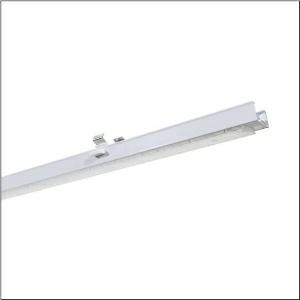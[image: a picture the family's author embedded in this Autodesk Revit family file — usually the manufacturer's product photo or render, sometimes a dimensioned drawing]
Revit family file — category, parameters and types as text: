
# Revit family: trunking_flex_31_51re11db49b
name_source: partatom
category: Lighting Fixtures
units: mm (PartAtom-declared; Revit-internal decimal feet)

## family parameters
Cut with Voids When Loaded = No
Host = Face
Light Source = No
Part Type = Normal
Room Calculation Point = No
Round Connector Dimension = Use Diameter
Shared = No

## types (1)
- Trunking Flex 31 (1 x LED, 8900 lm, 53 W, 4000K)
    Apparent Load = 53 VA
    CIE Flux Codes = 83 93 98 100 100
    Color Rendering = 80
    Color Temperature = 4000K
    Default Elevation = 1800 mm
    Description = Trunking Flex 31, luminaire insert, of extruded aluminium section, coated, traffic white (RAL 9016), length: 1.472mm, width: 91mm, height: 53mm, LED rated luminous flux: 8.900lm, light colour: 840, control gear: DALI 2, with system connector: socket, mains connection: 220..240V, AC, 50/60Hz, rated input power: 53W, primary light control with lens, of plastic, primary optical cover: cover, of PMMA, light emission: direct distribution, protection rating (complete): IP20, insulation class (complete): insulation class I (protective earthing), certification: CE, UKCA, impact resistance: IK02, permissible ambient temperature for indoor applications: -20..+40°C, packaging unit: 1 piece
    Height = 58 mm
    Lamp = 1 x LED
    Lamp Light Flux = 8900 lm
    Lamp Power = 53 W
    Lamp count = 1
    Length = 1472 mm
    Luminous efficacy = 168 lm/W
    Manufacturer = Siteco
    ModVariant = No
    Model = 51RE11DB49B
    Mounting Place = Ceiling
    Mounting Type = Pendant
    Number of Poles = 1
    OnlyDefault = Yes
    Power Factor = 1
    Product Name = Trunking Flex 31
    Product group = luminaire insert | ceiling pendant
    ProductGroupID = 902
    Protection Class = Protection class I
    Protection Degree = IP 20
    RLX_Detail_Level = 1
    RLX_Emergency_Light_Flux = 0 lm
    RLX_Emergency_Type = 0
    RLX_Emergency_Type_DB = No
    RlxData = <blob elided: 19457 chars, md5=ffc54437>
    Socket = socket
    Standby Power = 0 W
    System Light Flux = 8900 lm
    System Power = 53 W
    Type Comments = Product without accessories
    Type Image = l_1266702.jpg
    URL = http://relux.com
    VarID = ---
    Voltage = 0 V
    Weight = 0.00 kg
    Width = 65 mm

## geometry (parser evidence)
native form markers: Blend x4, Sweep x11
no freeform markers — native parametric forms only
